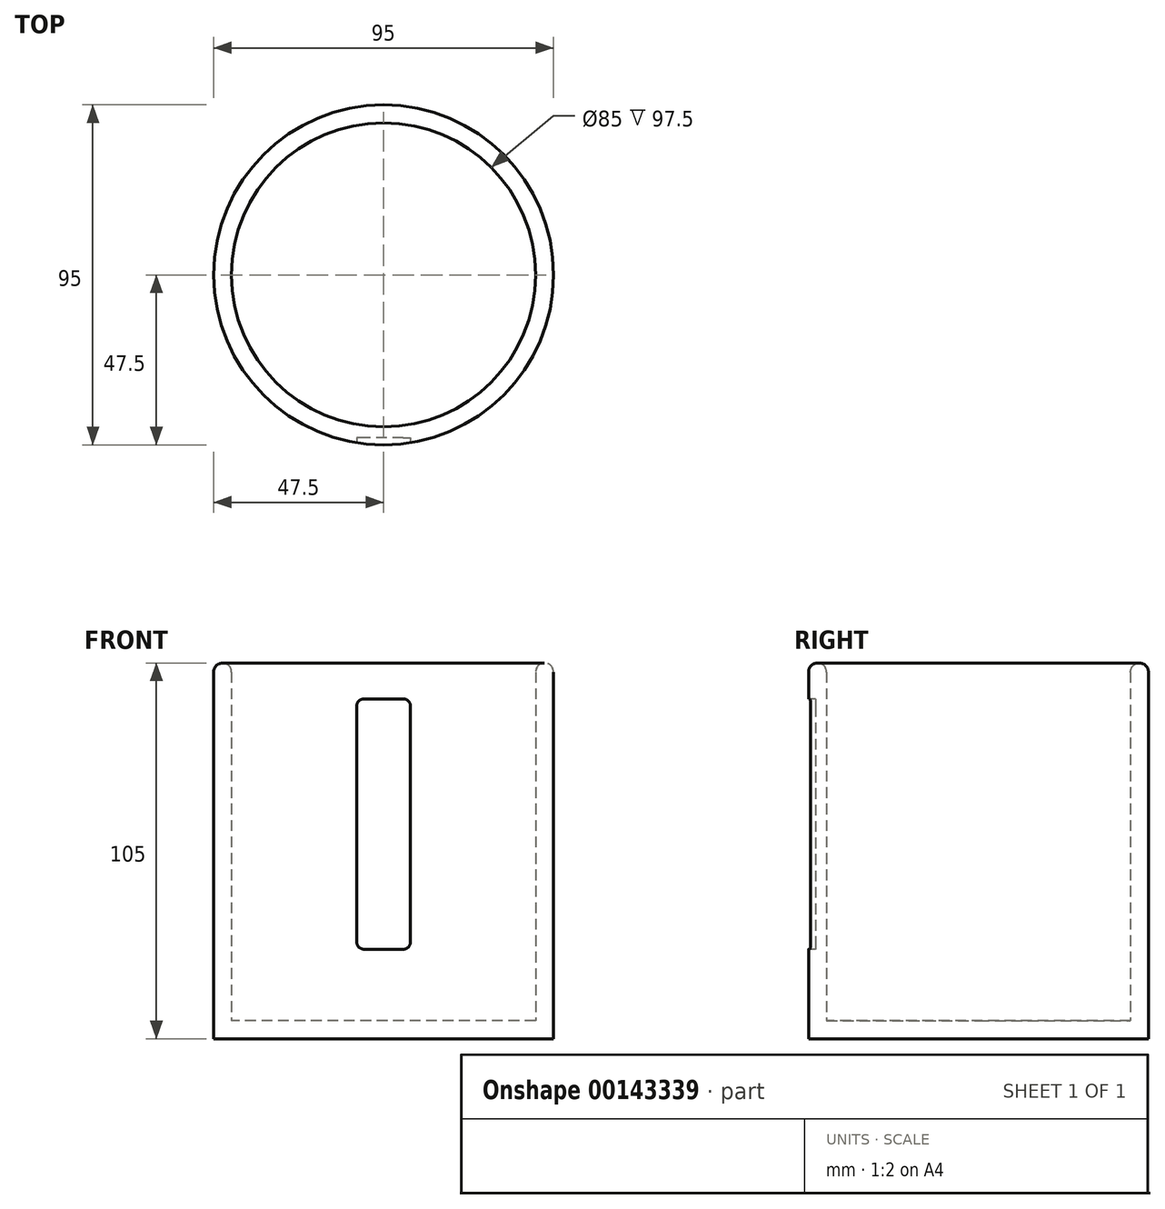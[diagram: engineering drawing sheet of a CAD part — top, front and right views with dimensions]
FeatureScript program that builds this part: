
annotation { "Feature Type Name" : "Feature", "Feature Type Description" : "" }
export const myFeature = defineFeature(function(context is Context, id is Id, definition is map)
    precondition{}
    {
        {
            var Q0;
            Q0=qCreatedBy(makeId("Top.planeOp"),FACE);
            var sketch = newSketch(context, id + "F0", { "sketchPlane" : qUnion([Q0])});
            skCircle(sketch, "E0", {"center": v(0, 0) * mm, "radius": 47.5 * mm});
            skSolve(sketch);
        }
        {
            var Q0;
            Q0 = qSketchRegion(id + "F0", true);
            extrude(context, id + "F1", {"entities" : qUnion([Q0]), "depth" : 5 * mm});
        }
        {
            var Q0;
            Q0=makeQuery(id+"F1.opExtrude","CAP_FACE",FACE,{"disambiguationData":[OSD([sQuery(id+"F0.wireOp",EDGE,"E0")])],"isStart":false});
            var sketch = newSketch(context, id + "F2", { "sketchPlane" : qUnion([Q0])});
            skCircle(sketch, "E1", {"center": v(0, 0) * mm, "radius": 47.5 * mm});
            skCircle(sketch, "E2", {"center": v(0, 0) * mm, "radius": 42.5 * mm});
            skSolve(sketch);
        }
        {
            var Q0;
            Q0 = qSketchRegion(id + "F2", true);
            extrude(context, id + "F3", {"entities" : qUnion([Q0]), "operationType" : NewBodyOperationType.ADD, "depth" : 100 * mm});
        }
        {
            var Q0;
            Q0=qCreatedBy(makeId("Front.planeOp"),FACE);
            cPlane(context, id + "F4", {"entities" : qUnion([Q0]), "cplaneType" : CPlaneType.OFFSET, "offset" : 47.5 * mm, "width" : 150 * mm, "height" : 150 * mm});
        }
        {
            var Q0;
            Q0=qCreatedBy(id+"F4.planeOp",FACE);
            var sketch = newSketch(context, id + "F5", { "sketchPlane" : qUnion([Q0])});
            skLineSegment(sketch, "E3.bottom", {"start": v(5.5, 95) * mm, "end": v(-5.5, 95) * mm});
            skLineSegment(sketch, "E3.top", {"start": v(5.5, 25) * mm, "end": v(-5.5, 25) * mm});
            skLineSegment(sketch, "E3.left", {"start": v(7.5, 93) * mm, "end": v(7.5, 27) * mm});
            skLineSegment(sketch, "E3.right", {"start": v(-7.5, 93) * mm, "end": v(-7.5, 27) * mm});
            skPoint(sketch, "E4.visualSharp", {"position": v(7.5, 95) * mm});
            skArc(sketch, "E4.filletArc", {"start": v(7.5, 93) * mm, "mid": v(6.91, 94.41) * mm, "end": v(5.5, 95) * mm});
            skPoint(sketch, "E5.visualSharp", {"position": v(-7.5, 95) * mm});
            skArc(sketch, "E5.filletArc", {"start": v(-5.5, 95) * mm, "mid": v(-6.91, 94.41) * mm, "end": v(-7.5, 93) * mm});
            skPoint(sketch, "E6.visualSharp", {"position": v(-7.5, 25) * mm});
            skArc(sketch, "E6.filletArc", {"start": v(-7.5, 27) * mm, "mid": v(-6.91, 25.59) * mm, "end": v(-5.5, 25) * mm});
            skPoint(sketch, "E7.visualSharp", {"position": v(7.5, 25) * mm});
            skArc(sketch, "E7.filletArc", {"start": v(5.5, 25) * mm, "mid": v(6.91, 25.59) * mm, "end": v(7.5, 27) * mm});
            skLineSegment(sketch, "E8", {"start": v(0, 0) * mm, "end": v(0, 20.18) * mm, "construction": true});
            skSolve(sketch);
        }
        {
            var Q0;
            Q0 = qSketchRegion(id + "F5", true);
            extrude(context, id + "F6", {"entities" : qUnion([Q0]), "operationType" : NewBodyOperationType.REMOVE, "oppositeDirection" : true, "depth" : 2 * mm});
        }
        {
            var Q0;
            Q0=makeQuery(id+"F6.boolean.opBoolean","COPY",FACE,{"derivedFrom":makeQuery(id+"F6.opExtrude","CAP_FACE",FACE,{"disambiguationData":[OSD([sQuery(id+"F5.wireOp",EDGE,"E3.bottom"),sQuery(id+"F5.wireOp",EDGE,"E3.top"),sQuery(id+"F5.wireOp",EDGE,"E3.left"),sQuery(id+"F5.wireOp",EDGE,"E3.right"),sQuery(id+"F5.wireOp",EDGE,"E4.filletArc"),sQuery(id+"F5.wireOp",EDGE,"E5.filletArc"),sQuery(id+"F5.wireOp",EDGE,"E6.filletArc"),sQuery(id+"F5.wireOp",EDGE,"E7.filletArc")])],"isStart":false})});
            var sketch = newSketch(context, id + "F7", { "sketchPlane" : qUnion([Q0])});
            skPoint(sketch, "E9", {"position": v(0, 86) * mm});
            skPoint(sketch, "E10", {"position": v(0, 70) * mm});
            skPoint(sketch, "E11", {"position": v(0, 50) * mm});
            skPoint(sketch, "E12", {"position": v(0, 34) * mm});
            skSolve(sketch);
        }
        {
            var Q0;
            Q0=makeQuery(id+"F3.opExtrude","CAP_EDGE",EDGE,{"disambiguationData":[OSD([sQuery(id+"F2.wireOp",EDGE,"E1")])],"isStart":false});
            var Q1;
            Q1=makeQuery(id+"F3.opExtrude","CAP_EDGE",EDGE,{"disambiguationData":[OSD([sQuery(id+"F2.wireOp",EDGE,"E2")])],"isStart":false});
            fillet(context, id + "F8", {"entities" : qUnion([Q0, Q1]), "radius" : 2.5 * mm, "tangentPropagation" : true, "allowEdgeOverflow" : false});
        }
    });
